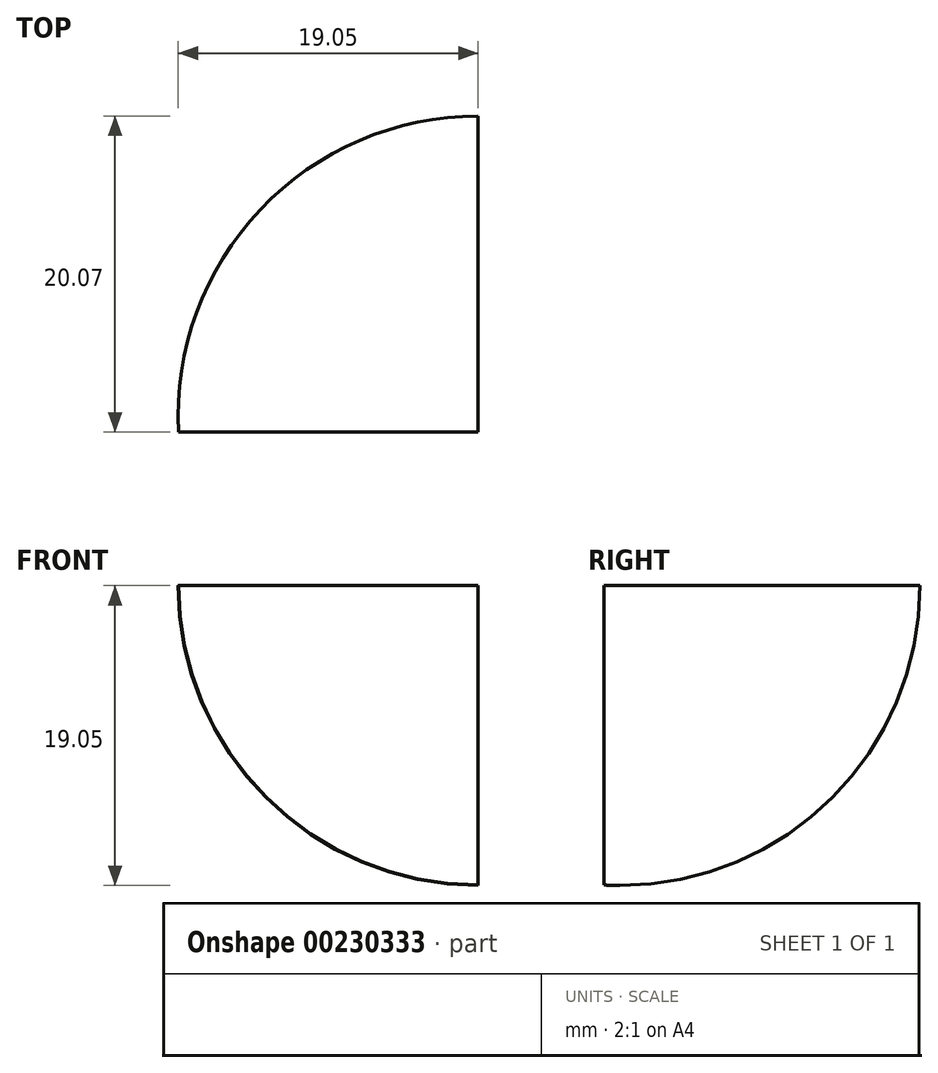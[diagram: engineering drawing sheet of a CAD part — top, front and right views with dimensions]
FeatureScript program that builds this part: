
annotation { "Feature Type Name" : "Feature", "Feature Type Description" : "" }
export const myFeature = defineFeature(function(context is Context, id is Id, definition is map)
    precondition{}
    {
        {
            var Q0;
            Q0=qCreatedBy(makeId("Front.planeOp"),FACE);
            cPlane(context, id + "F0", {"entities" : qUnion([Q0]), "cplaneType" : CPlaneType.OFFSET, "offset" : 1.02 * mm, "oppositeDirection" : true, "width" : 150 * mm, "height" : 150 * mm});
        }
        {
            var Q0;
            Q0=qCreatedBy(id+"F0.planeOp",FACE);
            var sketch = newSketch(context, id + "F1", { "sketchPlane" : qUnion([Q0])});
            skLineSegment(sketch, "E0", {"start": v(-1.02, -20.07) * mm, "end": v(-1.02, 18.03) * mm});
            skPoint(sketch, "E1", {"position": v(-1.02, -1.02) * mm});
            skArc(sketch, "E2", {"start": v(-1.02, 18.03) * mm, "mid": v(-20.07, -1.02) * mm, "end": v(-1.02, -20.07) * mm});
            skSolve(sketch);
        }
        {
            var Q0;
            Q0=makeQuery(id+"F1.imprint","IMPRINT",FACE,{"disambiguationData":[TD([[makeQuery(id+"F1.imprint","IMPRINT",EDGE,{"derivedFrom":sQuery(id+"F1.wireOp",EDGE,"E0")}),1.0]])]});
            var Q1;
            Q1=sQuery(id+"F1.wireOp",EDGE,"E0");
            revolve(context, id + "F2", {"entities" : qUnion([Q0]), "axis" : qUnion([Q1]), "revolveType" : RevolveType.FULL});
        }
        {
            var Q0;
            Q0=qCreatedBy(makeId("Front.planeOp"),FACE);
            var sketch = newSketch(context, id + "F3", { "sketchPlane" : qUnion([Q0])});
            skCircle(sketch, "E3", {"center": v(-1.02, -1.02) * mm, "radius": 19.05 * mm});
            skLineSegment(sketch, "E4", {"start": v(-1.02, -1.02) * mm, "end": v(-20.07, -1.02) * mm});
            skLineSegment(sketch, "E5", {"start": v(-1.02, -1.02) * mm, "end": v(-1.02, -20.07) * mm});
            skSolve(sketch);
        }
        {
            var Q0;
            {var subQ0=sQuery(id+"F3.wireOp",EDGE,"E4");Q0=makeQuery(id+"F3.imprint","IMPRINT",FACE,{"disambiguationData":[TD([[makeQuery(id+"F3.imprint","IMPRINT",EDGE,{"derivedFrom":subQ0}),1.0]])]});}
            extrude(context, id + "F4", {"entities" : qUnion([Q0]), "operationType" : NewBodyOperationType.REMOVE, "oppositeDirection" : true, "depth" : 25 * mm});
        }
    });
